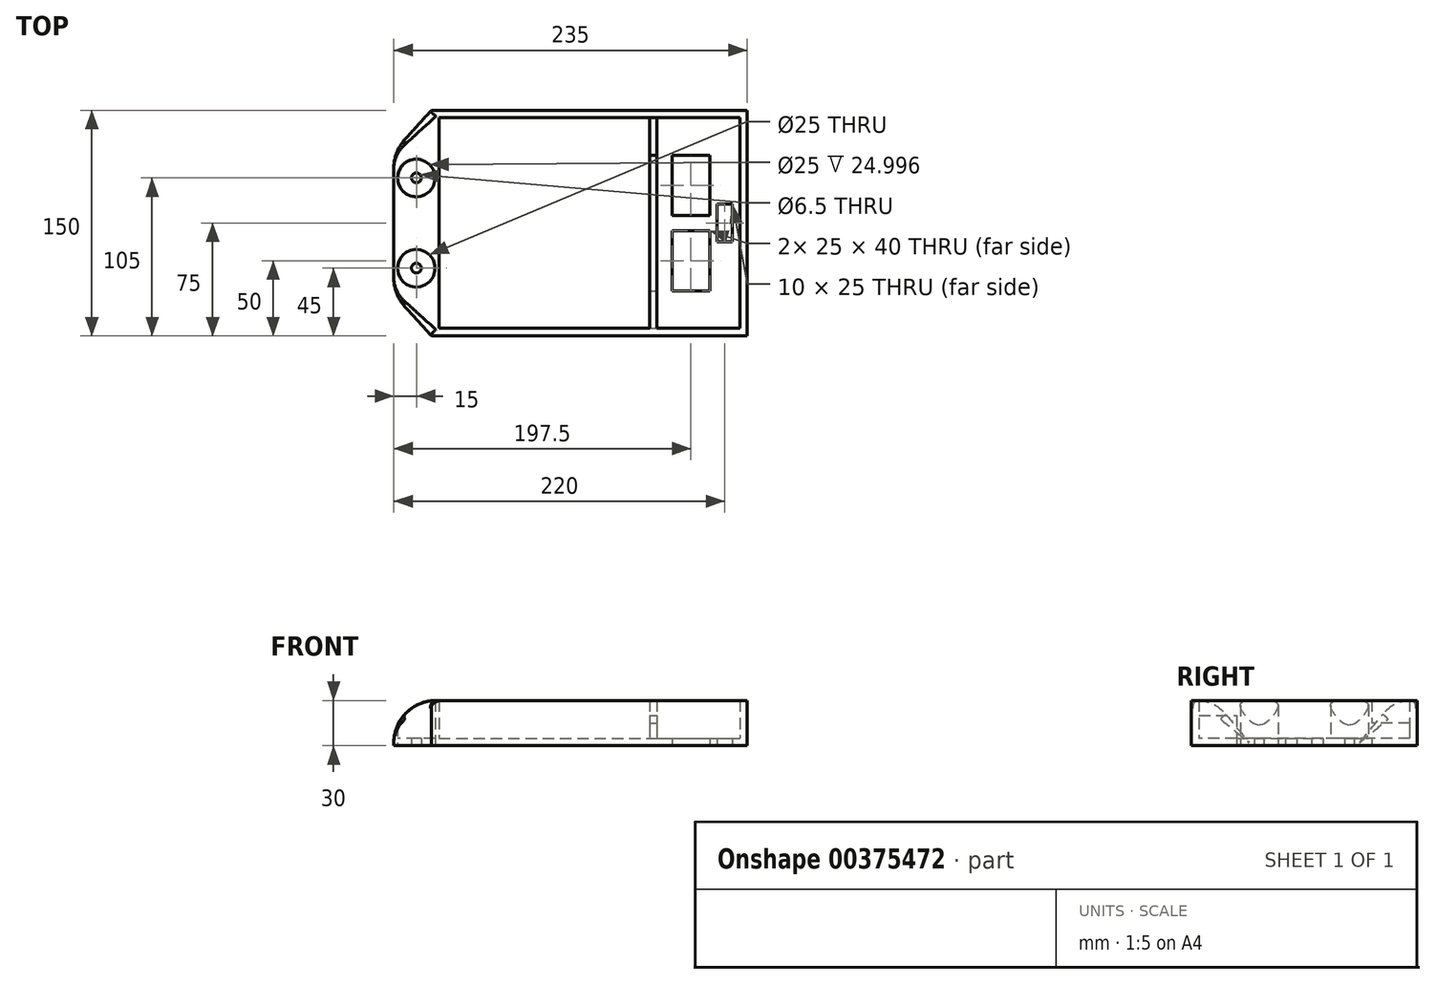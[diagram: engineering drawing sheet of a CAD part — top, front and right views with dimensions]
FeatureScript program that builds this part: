
annotation { "Feature Type Name" : "Feature", "Feature Type Description" : "" }
export const myFeature = defineFeature(function(context is Context, id is Id, definition is map)
    precondition{}
    {
        {
            var Q0;
            Q0=qCreatedBy(makeId("Top.planeOp"),FACE);
            var sketch = newSketch(context, id + "F0", { "sketchPlane" : qUnion([Q0])});
            skLineSegment(sketch, "E0.bottom", {"start": v(-92.5, 75) * mm, "end": v(117.5, 75) * mm});
            skLineSegment(sketch, "E0.top", {"start": v(-117.5, 0) * mm, "end": v(117.5, 0) * mm, "construction": true});
            skLineSegment(sketch, "E0.left", {"start": v(-117.5, 47.5) * mm, "end": v(-117.5, 0) * mm});
            skLineSegment(sketch, "E0.right", {"start": v(117.5, 75) * mm, "end": v(117.5, 0) * mm});
            skLineSegment(sketch, "E1", {"start": v(-117.5, 47.5) * mm, "end": v(-92.5, 75) * mm});
            skCircle(sketch, "E2", {"center": v(-102.5, 30) * mm, "radius": 3.25 * mm});
            skLineSegment(sketch, "E3.bottom", {"start": v(67.5, 45) * mm, "end": v(92.5, 45) * mm});
            skLineSegment(sketch, "E3.top", {"start": v(67.5, 5) * mm, "end": v(92.5, 5) * mm});
            skLineSegment(sketch, "E3.left", {"start": v(67.5, 45) * mm, "end": v(67.5, 5) * mm});
            skLineSegment(sketch, "E3.right", {"start": v(92.5, 45) * mm, "end": v(92.5, 5) * mm});
            skLineSegment(sketch, "E4.top", {"start": v(97.5, 12.5) * mm, "end": v(107.5, 12.5) * mm});
            skLineSegment(sketch, "E4.left", {"start": v(97.5, 0) * mm, "end": v(97.5, 12.5) * mm});
            skLineSegment(sketch, "E4.right", {"start": v(107.5, 0) * mm, "end": v(107.5, 12.5) * mm});
            skLineSegment(sketch, "E5.bottom", {"start": v(-87.5, 70) * mm, "end": v(112.5, 70) * mm});
            skLineSegment(sketch, "E5.left", {"start": v(-87.5, 70) * mm, "end": v(-87.5, 0) * mm});
            skLineSegment(sketch, "E5.right", {"start": v(112.5, 70) * mm, "end": v(112.5, 0) * mm});
            skLineSegment(sketch, "E6.left", {"start": v(52.5, 70) * mm, "end": v(52.5, 0) * mm});
            skLineSegment(sketch, "E6.right", {"start": v(57.5, 70) * mm, "end": v(57.5, 0) * mm});
            skLineSegment(sketch, "E7", {"start": v(52.5, 45) * mm, "end": v(57.5, 45) * mm});
            skLineSegment(sketch, "E8.MirrorCS", {"start": v(52.5, -70) * mm, "end": v(57.5, -70) * mm});
            skLineSegment(sketch, "E9.MirrorCS", {"start": v(107.5, 0) * mm, "end": v(107.5, -12.5) * mm});
            skLineSegment(sketch, "E10.MirrorCS", {"start": v(97.5, -12.5) * mm, "end": v(107.5, -12.5) * mm});
            skLineSegment(sketch, "E11.MirrorCS", {"start": v(97.5, 0) * mm, "end": v(97.5, -12.5) * mm});
            skLineSegment(sketch, "E12.MirrorCS", {"start": v(52.5, 0) * mm, "end": v(112.5, 0) * mm});
            skCircle(sketch, "E13.MirrorC", {"center": v(-102.5, -30) * mm, "radius": 3.25 * mm});
            skLineSegment(sketch, "E14.MirrorCS", {"start": v(52.5, -45) * mm, "end": v(57.5, -45) * mm});
            skLineSegment(sketch, "E15.MirrorCS", {"start": v(52.5, -70) * mm, "end": v(52.5, 0) * mm});
            skLineSegment(sketch, "E16.MirrorCS", {"start": v(-87.5, -70) * mm, "end": v(112.5, -70) * mm});
            skLineSegment(sketch, "E17.MirrorCS", {"start": v(-87.5, -70) * mm, "end": v(-87.5, 0) * mm});
            skLineSegment(sketch, "E18.MirrorCS", {"start": v(-92.5, -75) * mm, "end": v(117.5, -75) * mm});
            skLineSegment(sketch, "E19.MirrorCS", {"start": v(-117.5, -47.5) * mm, "end": v(-117.5, 0) * mm});
            skLineSegment(sketch, "E20.MirrorCS", {"start": v(117.5, -75) * mm, "end": v(117.5, 0) * mm});
            skLineSegment(sketch, "E21.MirrorCS", {"start": v(-117.5, -47.5) * mm, "end": v(-92.5, -75) * mm});
            skLineSegment(sketch, "E22.MirrorCS", {"start": v(67.5, -45) * mm, "end": v(92.5, -45) * mm});
            skLineSegment(sketch, "E23.MirrorCS", {"start": v(67.5, -5) * mm, "end": v(92.5, -5) * mm});
            skLineSegment(sketch, "E24.MirrorCS", {"start": v(67.5, -45) * mm, "end": v(67.5, -5) * mm});
            skLineSegment(sketch, "E25.MirrorCS", {"start": v(112.5, -70) * mm, "end": v(112.5, 0) * mm});
            skLineSegment(sketch, "E26.MirrorCS", {"start": v(92.5, -45) * mm, "end": v(92.5, -5) * mm});
            skLineSegment(sketch, "E27.MirrorCS", {"start": v(57.5, -70) * mm, "end": v(57.5, 0) * mm});
            skCircle(sketch, "E28", {"center": v(-102.5, 30) * mm, "radius": 12.5 * mm});
            skCircle(sketch, "E29.MirrorC", {"center": v(-102.5, -30) * mm, "radius": 12.5 * mm});
            skSolve(sketch);
        }
        {
            var Q0;
            Q0=makeQuery(id+"F0.imprint","IMPRINT",FACE,{"disambiguationData":[TD([[makeQuery(id+"F0.imprint","IMPRINT",EDGE,{"derivedFrom":sQuery(id+"F0.wireOp",EDGE,"E0.bottom")}),-1.0]])]});
            extrude(context, id + "F1", {"entities" : qUnion([Q0]), "depth" : 30 * mm});
        }
        {
            var Q0;
            {var subQ4=sQuery(id+"F0.wireOp",EDGE,"E5.left");Q0=makeQuery(id+"F0.imprint","IMPRINT",FACE,{"disambiguationData":[TD([[makeQuery(id+"F0.imprint","IMPRINT",EDGE,{"derivedFrom":subQ4}),1.0]])]});}
            var Q1;
            Q1=makeQuery(id+"F0.imprint","IMPRINT",FACE,{"disambiguationData":[TD([[makeQuery(id+"F0.imprint","IMPRINT",EDGE,{"derivedFrom":sQuery(id+"F0.wireOp",EDGE,"E3.bottom")}),1.0]])]});
            var Q2;
            {var subQ1=sQuery(id+"F0.wireOp",EDGE,"E9.MirrorCS");Q2=makeQuery(id+"F0.imprint","IMPRINT",FACE,{"disambiguationData":[TD([[makeQuery(id+"F0.imprint","IMPRINT",EDGE,{"derivedFrom":subQ1}),1.0]])]});}
            extrude(context, id + "F2", {"entities" : qUnion([Q0, Q1, Q2]), "operationType" : NewBodyOperationType.ADD, "depth" : 5 * mm});
        }
        {
            var Q0;
            {var subQ0=sQuery(id+"F0.wireOp",EDGE,"E14.MirrorCS");Q0=makeQuery(id+"F0.imprint","IMPRINT",FACE,{"disambiguationData":[TD([[makeQuery(id+"F0.imprint","IMPRINT",EDGE,{"derivedFrom":subQ0}),-1.0]])]});}
            var Q1;
            {var subQ5=sQuery(id+"F0.wireOp",EDGE,"E14.MirrorCS");Q1=makeQuery(id+"F0.imprint","IMPRINT",FACE,{"disambiguationData":[TD([[makeQuery(id+"F0.imprint","IMPRINT",EDGE,{"derivedFrom":subQ5}),1.0]])]});}
            var Q2;
            {var subQ3=sQuery(id+"F0.wireOp",EDGE,"E7");Q2=makeQuery(id+"F0.imprint","IMPRINT",FACE,{"disambiguationData":[TD([[makeQuery(id+"F0.imprint","IMPRINT",EDGE,{"derivedFrom":subQ3}),-1.0]])]});}
            var Q3;
            {var subQ5=sQuery(id+"F0.wireOp",EDGE,"E7");Q3=makeQuery(id+"F0.imprint","IMPRINT",FACE,{"disambiguationData":[TD([[makeQuery(id+"F0.imprint","IMPRINT",EDGE,{"derivedFrom":subQ5}),1.0]])]});}
            extrude(context, id + "F3", {"entities" : qUnion([Q0, Q1, Q2, Q3]), "operationType" : NewBodyOperationType.ADD, "depth" : 30 * mm});
        }
        {
            var Q0;
            {var subQ0=sQuery(id+"F0.wireOp",EDGE,"E14.MirrorCS");Q0=makeQuery(id+"F0.imprint","IMPRINT",FACE,{"disambiguationData":[TD([[makeQuery(id+"F0.imprint","IMPRINT",EDGE,{"derivedFrom":subQ0}),-1.0]])]});}
            extrude(context, id + "F4", {"entities" : qUnion([Q0]), "operationType" : NewBodyOperationType.REMOVE, "depth" : 20 * mm});
        }
        {
            var Q0;
            {var subQ0=sQuery(id+"F0.wireOp",EDGE,"E14.MirrorCS");Q0=makeQuery(id+"F0.imprint","IMPRINT",FACE,{"disambiguationData":[TD([[makeQuery(id+"F0.imprint","IMPRINT",EDGE,{"derivedFrom":subQ0}),-1.0]])]});}
            extrude(context, id + "F5", {"entities" : qUnion([Q0]), "operationType" : NewBodyOperationType.ADD, "depth" : 5 * mm});
        }
        {
            var Q0;
            {var subQ5=sQuery(id+"F0.wireOp",EDGE,"E7");Q0=makeQuery(id+"F0.imprint","IMPRINT",FACE,{"disambiguationData":[TD([[makeQuery(id+"F0.imprint","IMPRINT",EDGE,{"derivedFrom":subQ5}),1.0]])]});}
            extrude(context, id + "F6", {"entities" : qUnion([Q0]), "operationType" : NewBodyOperationType.REMOVE, "depth" : 30 * mm});
        }
        {
            var Q0;
            {var subQ5=sQuery(id+"F0.wireOp",EDGE,"E7");Q0=makeQuery(id+"F0.imprint","IMPRINT",FACE,{"disambiguationData":[TD([[makeQuery(id+"F0.imprint","IMPRINT",EDGE,{"derivedFrom":subQ5}),1.0]])]});}
            extrude(context, id + "F7", {"entities" : qUnion([Q0]), "operationType" : NewBodyOperationType.ADD, "depth" : 15 * mm});
        }
        {
            var Q0;
            Q0=makeQuery(id+"F0.imprint","IMPRINT",FACE,{"disambiguationData":[TD([[makeQuery(id+"F0.imprint","IMPRINT",EDGE,{"derivedFrom":sQuery(id+"F0.wireOp",EDGE,"E13.MirrorC")}),1.0]])]});
            var Q1;
            Q1=makeQuery(id+"F0.imprint","IMPRINT",FACE,{"disambiguationData":[TD([[makeQuery(id+"F0.imprint","IMPRINT",EDGE,{"derivedFrom":sQuery(id+"F0.wireOp",EDGE,"E2")}),-1.0]])]});
            extrude(context, id + "F8", {"entities" : qUnion([Q0, Q1]), "operationType" : NewBodyOperationType.ADD, "depth" : 5 * mm});
        }
        {
            var Q0;
            Q0=makeQuery(id+"F1.opExtrude","CAP_EDGE",EDGE,{"disambiguationData":[OSD([sQuery(id+"F0.wireOp",EDGE,"E21.MirrorCS")])],"isStart":false});
            var Q1;
            Q1=makeQuery(id+"F1.opExtrude","CAP_EDGE",EDGE,{"disambiguationData":[OSD([sQuery(id+"F0.wireOp",EDGE,"E1")])],"isStart":false});
            fillet(context, id + "F9", {"entities" : qUnion([Q0, Q1]), "radius" : 5 * mm, "tangentPropagation" : true, "allowEdgeOverflow" : false});
        }
        {
            var Q0;
            Q0=makeQuery(id+"F1.opExtrude","CAP_EDGE",EDGE,{"disambiguationData":[OSD([sQuery(id+"F0.wireOp",EDGE,"E0.left"),sQuery(id+"F0.wireOp",EDGE,"E19.MirrorCS")])],"isStart":false});
            fillet(context, id + "F10", {"entities" : qUnion([Q0]), "radius" : 28 * mm, "tangentPropagation" : true, "allowEdgeOverflow" : false});
        }
    });
